# Revit family: TR3010
name_source: partatom
category: Verbindungsmittel
units: mm (PartAtom-declared; Revit-internal decimal feet)

## family parameters
Arbeitsebenenbasiert = Nein
Beim Laden mit Abzugskörper schneiden = Nein
Gemeinsam genutzt = Nein
Immer vertikal = Nein
OmniClass-Nummer = 23.25.10.27.11.21
OmniClass-Titel = Reinforcement Couplers

## types (7) — shared parameters
Endenbearbeitung 1 = Mit Gewinde
Endenbearbeitung 2 = Mit Gewinde
Hersteller = Stahlwerk Annahütte Max Aicher GmbH Co.KG
Modell = TR 3010
TR3010-G_Vis = Ja
TR3010-L_Vis = Ja
TR3010-SW_Vis = Ja
Typenbild = TR3010.png
Typenkommentare = TR 3010 - Sechskantmuffe, lang
URL = http//:www.annahuette.com

## per-type parameters (varying)
| type | Außendurchmesser | Beschreibung | Einfassung Stab 1 | Einfassung Stab 2 | Gesamtlänge | Körper | Stabgröße 1 | Stabgröße 2 | TR3010-G | TR3010-L | TR3010-SW | TR3010-ød |
| TR 3010-ø18 | 36 mm  [stored 0.11811 ft] | TR3010-ø18 | 60 mm  [stored 0.19685 ft] | 60 mm  [stored 0.19685 ft] | 120 mm  [stored 0.393701 ft] | 0,78 kg | SAS 670 - ø18 | SAS 670 - ø18 | 0,78 kg | 120 mm  [stored 0.393701 ft] | 36 mm  [stored 0.11811 ft] | 18 mm  [stored 0.0590551 ft] |
| TR 3010-ø22 | 41 mm  [stored 0.134514 ft] | TR3010-ø22 | 68 mm | 68 mm | 135 mm  [stored 0.442913 ft] | 1,08 kg | SAS 670 - ø22 | SAS 670 - ø22 | 1,08 kg | 135 mm  [stored 0.442913 ft] | 41 mm  [stored 0.134514 ft] | 22 mm  [stored 0.0721785 ft] |
| TR 3010-ø25 | 46 mm  [stored 0.150919 ft] | TR3010-ø25 | 75 mm | 75 mm | 150 mm | 1,49 kg | SAS 670 - ø25 | SAS 670 - ø25 | 1,49 kg | 150 mm | 46 mm  [stored 0.150919 ft] | 25 mm  [stored 0.082021 ft] |
| TR 3010-ø28 | 50 mm  [stored 0.164042 ft] | TR3010-ø28 | 85 mm  [stored 0.278871 ft] | 85 mm  [stored 0.278871 ft] | 170 mm  [stored 0.557743 ft] | 1,96 kg | SAS 670 - ø28 | SAS 670 - ø28 | 1,96 kg | 170 mm  [stored 0.557743 ft] | 50 mm  [stored 0.164042 ft] | 28 mm  [stored 0.0918635 ft] |
| TR 3010-ø30 | 55 mm  [stored 0.180446 ft] | TR3010-ø30 | 93 mm | 93 mm | 185 mm  [stored 0.606955 ft] | 2,63 kg | SAS 670 - ø30 | SAS 670 - ø30 | 2,63 kg | 185 mm  [stored 0.606955 ft] | 55 mm  [stored 0.180446 ft] | 30 mm  [stored 0.0984252 ft] |
| TR 3010-ø35 | 60 mm  [stored 0.19685 ft] | TR3010-ø35 | 105 mm  [stored 0.344488 ft] | 105 mm  [stored 0.344488 ft] | 210 mm  [stored 0.688976 ft] | 3,36 kg | SAS 670 - ø35 | SAS 670 - ø35 | 3,36 kg | 210 mm  [stored 0.688976 ft] | 60 mm  [stored 0.19685 ft] | 35 mm  [stored 0.114829 ft] |
| TR 3010-ø43 | 79 mm | TR3010-ø43 | 123 mm | 123 mm | 245 mm  [stored 0.803806 ft] | 7,27 kg | SAS 670 - ø43 | SAS 670 - ø43 | 7,27 kg | 245 mm  [stored 0.803806 ft] | 79 mm | 43 mm  [stored 0.141076 ft] |

note: [stored X ft] marks values corroborated as IEEE doubles in the binary element streams (Revit-internal decimal feet)
